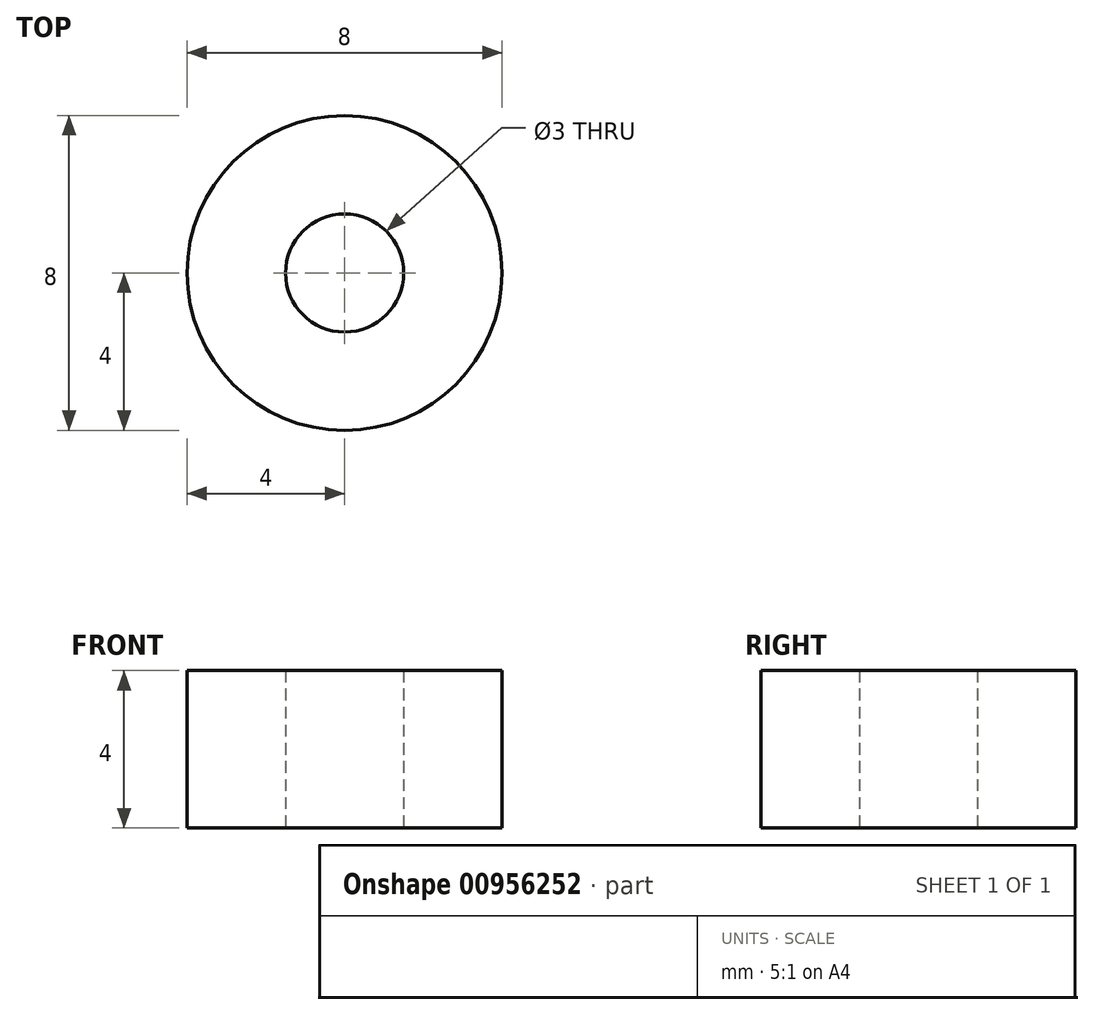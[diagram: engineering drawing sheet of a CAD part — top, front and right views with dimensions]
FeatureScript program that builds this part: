
annotation { "Feature Type Name" : "Feature", "Feature Type Description" : "" }
export const myFeature = defineFeature(function(context is Context, id is Id, definition is map)
    precondition{}
    {
        {
            var Q0;
            Q0=qCreatedBy(makeId("Top.planeOp"),FACE);
            var sketch = newSketch(context, id + "F0", { "sketchPlane" : qUnion([Q0])});
            skCircle(sketch, "E0", {"center": v(0, 0) * mm, "radius": 4 * mm});
            skCircle(sketch, "E1", {"center": v(0, 0) * mm, "radius": 1.5 * mm});
            skSolve(sketch);
        }
        {
            var Q0;
            Q0=qSketchRegion(id+"F0",true);
            extrude(context, id + "F1", {"entities" : qUnion([Q0]), "depth" : 4 * mm, "offsetDistance" : 25 * mm});
        }
    });
